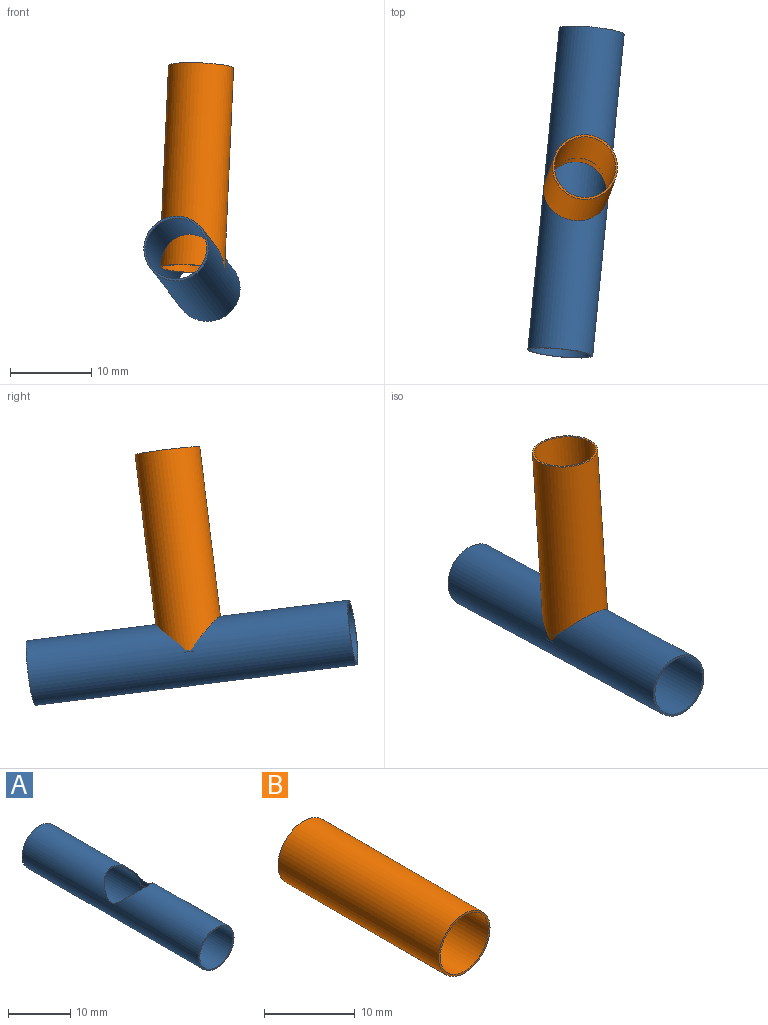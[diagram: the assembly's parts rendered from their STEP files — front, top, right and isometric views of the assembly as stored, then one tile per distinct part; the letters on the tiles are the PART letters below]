
ASSEMBLY  parts=2 mates=1
PART A: 7 faces, bbox 8x40x8 mm
  f0: cylinder r=3.75mm len=40mm, axis (0,1,0), area 879.1mm2, adj f1,f2,f4,f5,f6
  f1: plane 8x8mm, normal (0,-1,0), area 6.1mm2, adj f0,f3
  f2: plane 8x8mm, normal (0,1,0), area 6.1mm2, adj f0,f3
  f3: cylinder r=4mm len=40mm, axis (0,1,0), area 946.7mm2, adj f1,f2,f6
  f4: plane 2.14x0.15mm, normal (0,0,1), area 0.2mm2, adj f0,f6
  f5: plane 2.14x0.15mm, normal (0,0,1), area 0.2mm2, adj f0,f6
  f6: cylinder r=3.9mm len=7.8mm, axis (0,0,1), area 12.7mm2, adj f0,f3,f4,f5
PART B: 4 faces, bbox 8x25x8 mm
  f0: cylinder r=3.75mm len=25mm, axis (0,1,0), area 589mm2, adj f1,f2
  f1: plane 8x8mm, normal (0,-1,0), area 6.1mm2, adj f0,f3
  f2: plane 8x8mm, normal (0,1,0), area 6.1mm2, adj f0,f3
  f3: cylinder r=4mm len=25mm, axis (0,1,0), area 628.3mm2, adj f1,f2
PLACE A rot(axis=(-0.76,0.24,-0.61),9.3deg) t=(-5.32,-7.39,31.86)mm
PLACE B rot(axis=(1,-0.03,-0.07),83.1deg) t=(-3.39,12.36,29.36)mm
MATE fastened A.f4 <-> B.f3  axis (0.04,0.12,0.99) through (-3.39,12.36,29.36)mm
